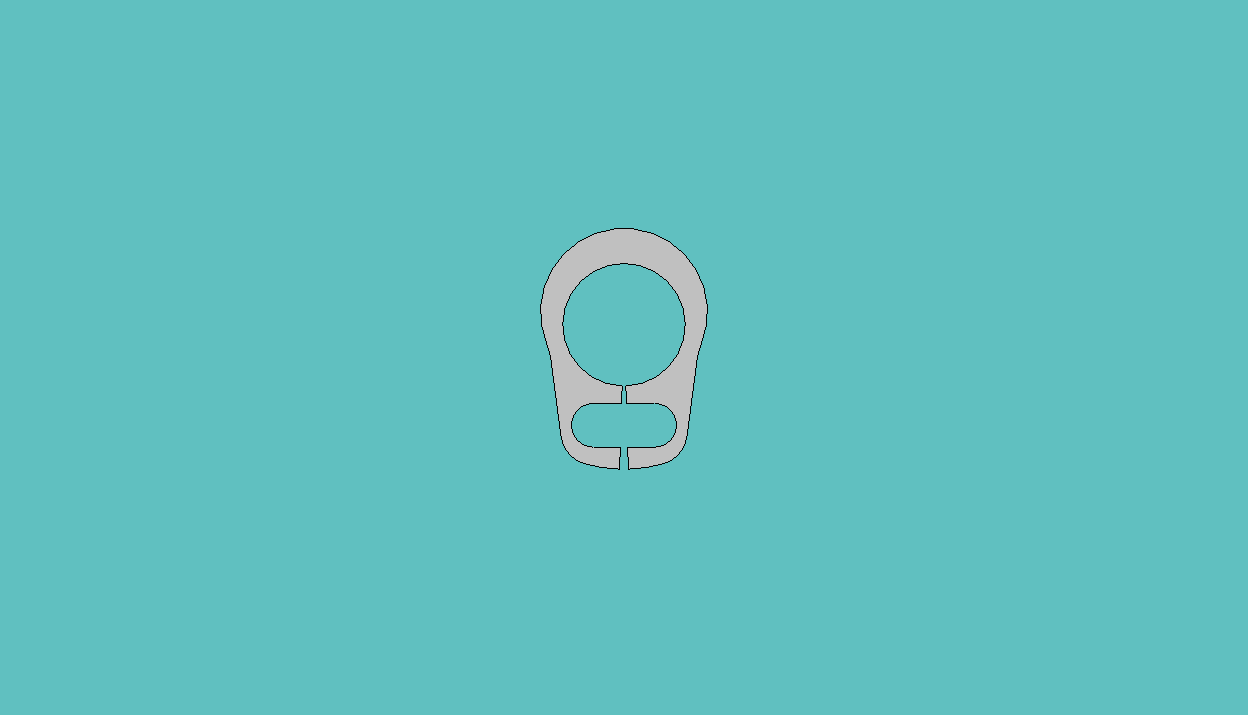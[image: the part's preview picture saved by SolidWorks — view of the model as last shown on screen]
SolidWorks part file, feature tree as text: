
SOLIDWORKS PART (.sldprt)
format: sldprt  version: not decoded by parser v0  size: 198,656 bytes
history: native  units: mm
features: extrude x5, sketch x4, plane x3, material x1, cut_extrude x1 (+8 scaffold rows collapsed)
feature tree (22):
  scaffold x8  (default folders/planes/origin — collapsed)
  material  "Matériau <non spécifié>"
  plane  "Plane1"
  plane  "Plane2"
  plane  "Plane3"
  sketch  "Clipboard"  dims[HoleDia=1.0mm ShaftDia=3.0mm LargeSection=0.8mm SmallSection=0.4mm LugSection=1.9mm]
  sketch  "BodySke"  dims[c1.GrooveDia=2.8mm c1.OutsideDia=~4.355353mm c1.TipRad=~0.23622mm c1.D3=2.6924mm c1.LugRad=3.3mm c1.HoleOffsetRad=2.4mm c1.HoleDia=1.0mm c2.D3=0.75mm c2.CavityRad=~1.532653mm c2.CavityWidth=3.0861mm c2.D1=~5.632972mm c3.D1=10.0deg c3.D2=~1.961375mm c4.D2=15.0deg c4.LargeRad=2.2mm c4.SmallRad=1.8mm c4.Gap=0.4445mm c4.D1=7.239mm c4.SmallAngle=~145.08307deg c5.D2=~3.638241mm c6.D2=15.0deg c6.HoleSpacing=1.4mm c6.Gap=0.4445mm c6.D1=2.5654mm c7.D1=~3.518715deg c7.Gap=0.2mm]
  extrude  "Body"  Depth=0.4mm Thickness=0.4mm
  sketch  "NotSke"
  cut_extrude  "Notch"  [1 undecoded]
  sketch  "UnlSke"
  extrude  "Unlug"  [1 undecoded]
  extrude  "ConfigurationName"  Depth=1 CopiedFlag=1
  extrude  "PartNumberID"  [1 undecoded]
  extrude  "ConfigurationName"  Depth=0 CopiedFlag=0
decode coverage: 5 of 10 modeling features carry decoded parameters
note: ~ marks probable driven/reference dimensions
note: 3 parameter values undecoded
summary: no parameter record found for 3 features
note: suppression state not decoded; provenance and decode notes live in map.json
